# Revit family: DF_НаконечникЗаземления_EZETEK
name_source: partatom
category: Соединительные детали воздуховодов
revit_build: Autodesk Revit 2017 (Build: 20170118_1100(x64)
units: mm (PartAtom-declared; Revit-internal decimal feet)

## family parameters
Всегда вертикально = Да
На основе рабочей плоскости = Нет
Общий = Нет
При загрузке вырезать с полостями = Нет
Размер круглого соединителя = Использовать радиус
Тип детали = Заглушка

## types (2) — shared parameters
ADSK_Версия Revit = 2017
ADSK_Единица измерения = Неспецифицируемое
ADSK_Завод-изготовитель = Неспецифицируемое
ADSK_Код изделия = Неспецифицируемое
ADSK_Марка = Неспецифицируемое
ADSK_Масса_Текст = Неспецифицируемое
ADSK_Материал = BIMLIB_Сталь_Оцинкованная_EZETEK
ADSK_Наименование = Неспецифицируемое
ADSK_Обозначение = Неспецифицируемое
URL = https://ezetek.ru
Группа модели = Наконечники заземления
Изготовитель = Ezetek
Описание = Зажим позволяет выполнить соединение в параллельном направлении полосы шириной до 40 мм и прутка 8-10 мм, а также осуществить переход с полосы на пруток.
zero-valued in all types: ADSK_Количество, ADSK_Масса

## per-type parameters (varying)
| type | Code1 | Тип |
| НаконечникЗаземления_НержавеющаяСталь_EZETEK | 2 мм | FA_НаконечникЗаземления_EZETEK : НаконечникЗаземления_НержавеющаяСталь_EZETEK |
| НаконечникЗаземления_Сталь_EZETEK | 1 мм | FA_НаконечникЗаземления_EZETEK : НаконечникЗаземления_Сталь_EZETEK |
